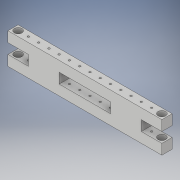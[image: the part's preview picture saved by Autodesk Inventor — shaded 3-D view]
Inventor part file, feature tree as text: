
AUTODESK INVENTOR PART (.ipt)
format: ipt  version: 2018 (Build 220112000, 112)  size: 164,864 bytes
history: native  units: in
note: dims shown in document units (in); Inventor stores cm internally (conversion verified against a paired STEP export)
features: extrude x3, sketch x3
ambient origin geometry x8: Origin, YZ Plane, XZ Plane, XY Plane, X Axis, Y Axis, Z Axis, Center Point
bodies: Solid1 (feature_tree)
feature tree (6):
  extrude  "Extrusion1"  Depth=3.0in
  extrude  "Extrusion6"  Depth=1.0in
  extrude  "Extrusion7"  Depth=1.0in
  sketch  "Sketch1"  dims[d0=15.0in d1=3.0in]
  sketch  "Sketch7"  dims[d2=1.0in d3=0.0in d34=1.0in]
  sketch  "Sketch8"  dims[d35=1.0in d36=1.0in d37=1.0in d38=0.0in d39=0.0in d40=3.0in d41=3.0in d42=2.0in d43=2.0in d44=1.0in d45=0.0in d46=0.1875in d47=0.5in d48=5.9055in d50=1.0in d51=0.3937in d53=1.0in d55=0.5in d56=3.0in d57=0.0in d58=0.75in d59=0.75in]
